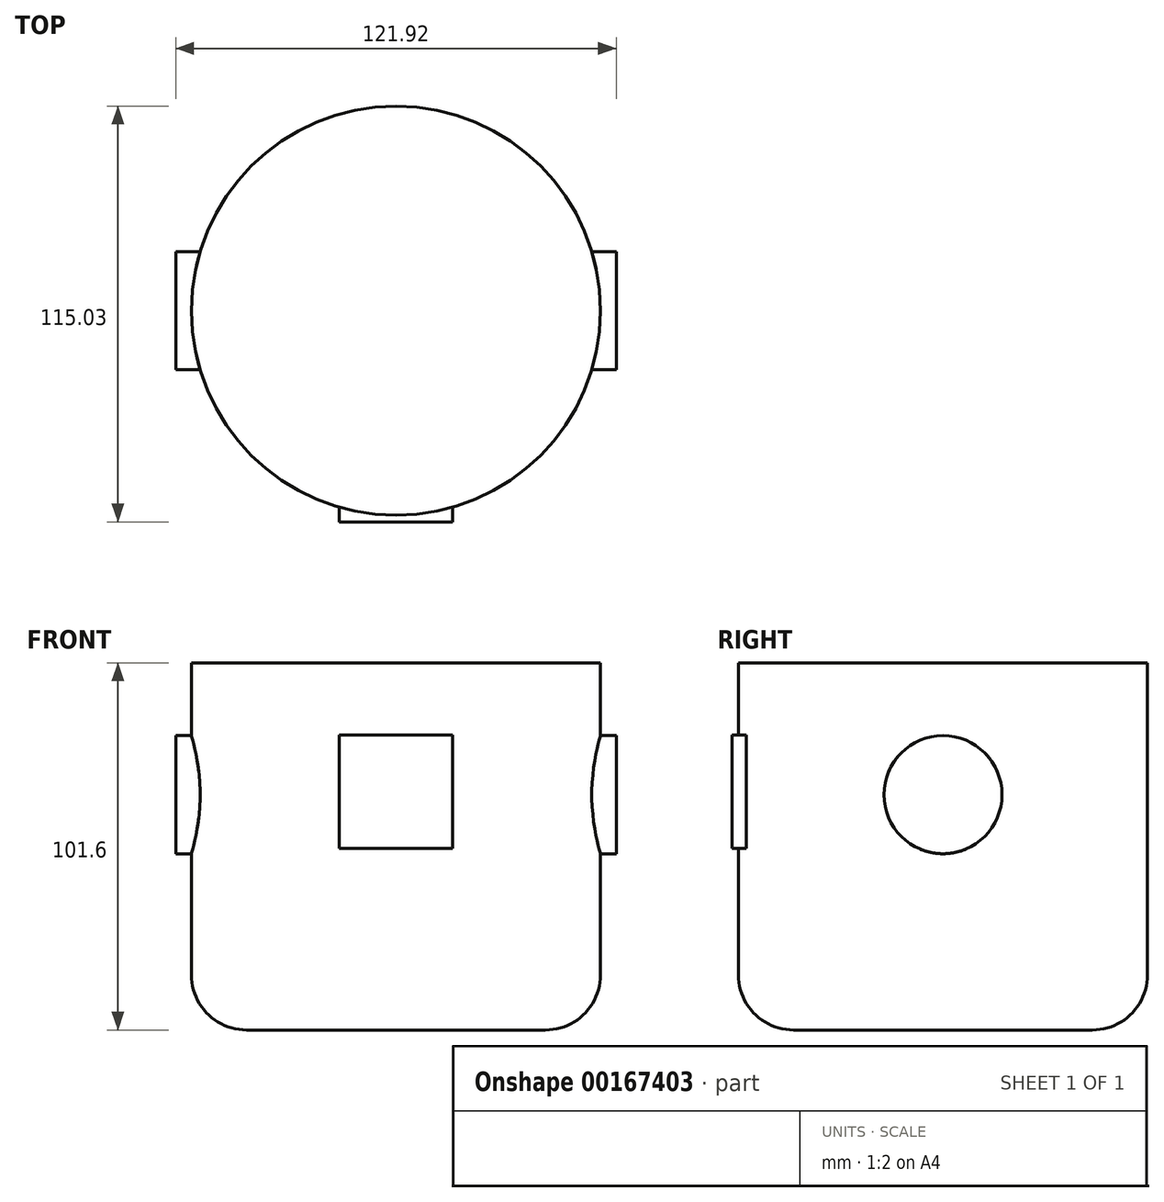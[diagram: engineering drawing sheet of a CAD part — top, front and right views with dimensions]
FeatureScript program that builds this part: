
annotation { "Feature Type Name" : "Feature", "Feature Type Description" : "" }
export const myFeature = defineFeature(function(context is Context, id is Id, definition is map)
    precondition{}
    {
        {
            var Q0;
            Q0=qCreatedBy(makeId("Top.planeOp"),FACE);
            var sketch = newSketch(context, id + "F0", { "sketchPlane" : qUnion([Q0])});
            skCircle(sketch, "E0", {"center": v(0, 0) * mm, "radius": 56.6 * mm});
            skSolve(sketch);
        }
        {
            var Q0;
            Q0=makeQuery(id+"F0.imprint","IMPRINT",FACE,{"disambiguationData":[TD([[makeQuery(id+"F0.imprint","IMPRINT",EDGE,{"derivedFrom":sQuery(id+"F0.wireOp",EDGE,"E0")}),1.0]])]});
            extrude(context, id + "F1", {"entities" : qUnion([Q0]), "depth" : 101.6 * mm});
        }
        {
            var Q0;
            Q0=makeQuery(id+"F1.opExtrude","CAP_EDGE",EDGE,{"disambiguationData":[OSD([sQuery(id+"F0.wireOp",EDGE,"E0")])],"isStart":true});
            fillet(context, id + "F2", {"entities" : qUnion([Q0]), "radius" : 15.24 * mm, "tangentPropagation" : true, "allowEdgeOverflow" : false});
        }
        {
            var Q0;
            Q0=qCreatedBy(makeId("Front.planeOp"),FACE);
            var sketch = newSketch(context, id + "F3", { "sketchPlane" : qUnion([Q0])});
            skLineSegment(sketch, "E1.bottom", {"start": v(15.7, 50.29) * mm, "end": v(-15.7, 50.29) * mm});
            skLineSegment(sketch, "E1.top", {"start": v(15.7, 81.67) * mm, "end": v(-15.7, 81.67) * mm});
            skLineSegment(sketch, "E1.left", {"start": v(15.7, 50.29) * mm, "end": v(15.7, 81.67) * mm});
            skLineSegment(sketch, "E1.right", {"start": v(-15.7, 50.29) * mm, "end": v(-15.7, 81.67) * mm});
            skPoint(sketch, "E1.middle", {"position": v(0, 65.98) * mm});
            skSolve(sketch);
        }
        {
            var Q0;
            Q0 = qSketchRegion(id + "F3", true);
            extrude(context, id + "F4", {"entities" : qUnion([Q0]), "operationType" : NewBodyOperationType.ADD, "depth" : 58.42 * mm});
        }
        {
            var Q0;
            Q0=qCreatedBy(makeId("Right.planeOp"),FACE);
            var sketch = newSketch(context, id + "F5", { "sketchPlane" : qUnion([Q0])});
            skPoint(sketch, "E2.middle", {"position": v(0, 65.1) * mm});
            skCircle(sketch, "E3", {"center": v(0, 65.1) * mm, "radius": 16.34 * mm});
            skSolve(sketch);
        }
        {
            var Q0;
            Q0 = qSketchRegion(id + "F5", true);
            extrude(context, id + "F6", {"entities" : qUnion([Q0]), "operationType" : NewBodyOperationType.ADD, "endBound" : BoundingType.SYMMETRIC, "depth" : 121.92 * mm});
        }
    });
